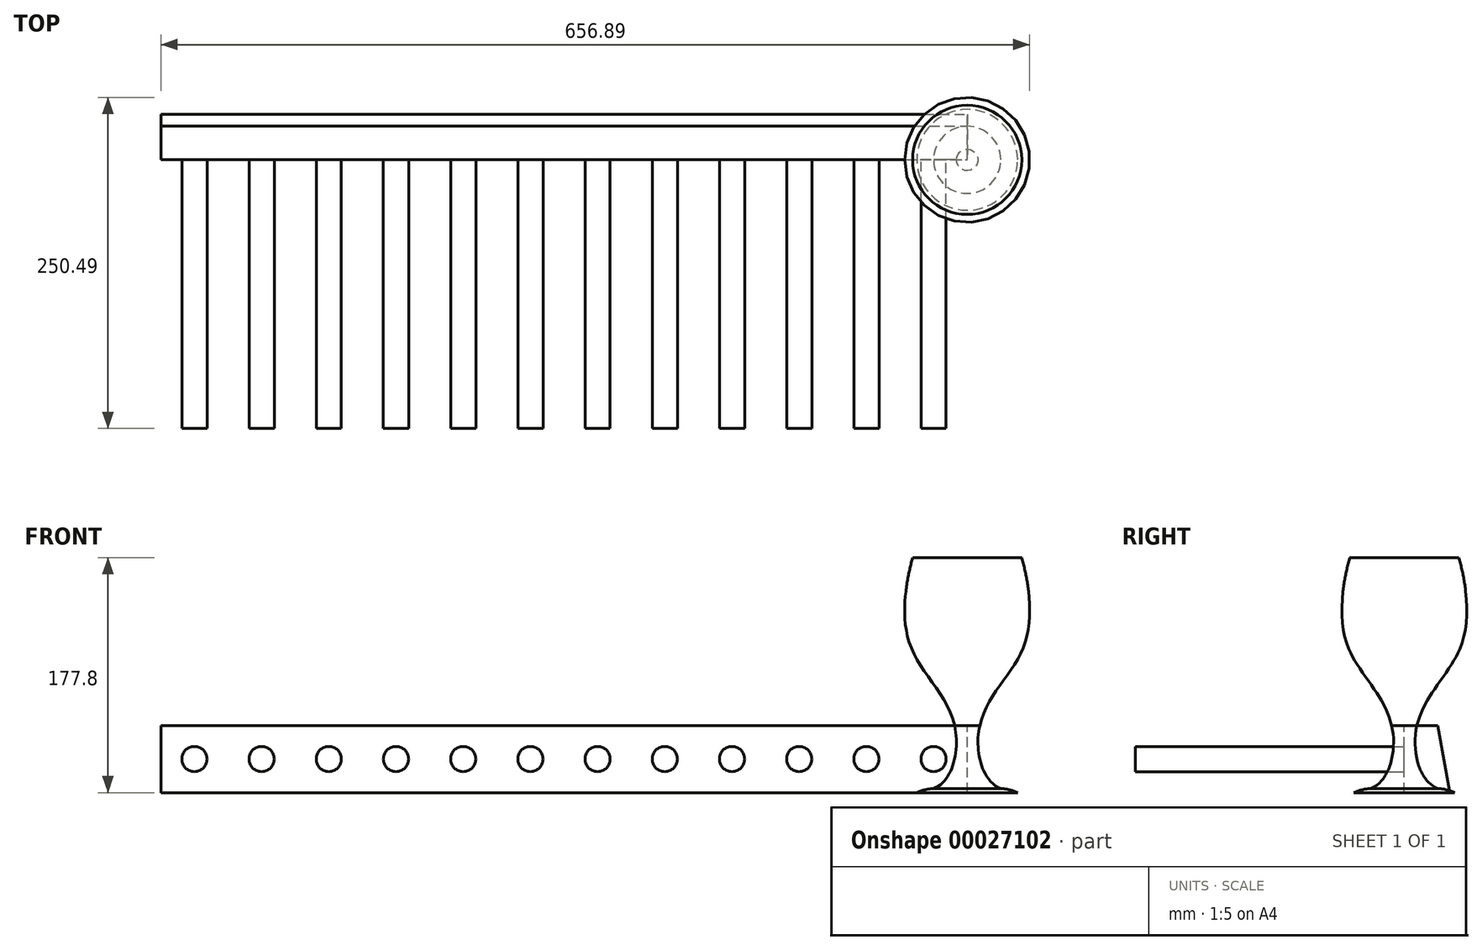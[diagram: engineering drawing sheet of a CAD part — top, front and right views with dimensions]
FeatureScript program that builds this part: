
annotation { "Feature Type Name" : "Feature", "Feature Type Description" : "" }
export const myFeature = defineFeature(function(context is Context, id is Id, definition is map)
    precondition{}
    {
        {
            var Q0;
            Q0=qCreatedBy(makeId("Front.planeOp"),FACE);
            var sketch = newSketch(context, id + "F0", { "sketchPlane" : qUnion([Q0])});
            skLineSegment(sketch, "E0", {"start": v(0, 0) * mm, "end": v(38.1, 0) * mm});
            skLineSegment(sketch, "E1", {"start": v(0, 0) * mm, "end": v(0, 177.8) * mm});
            skLineSegment(sketch, "E2", {"start": v(0, 177.8) * mm, "end": v(41.28, 177.8) * mm});
            skPoint(sketch, "E3", {"position": v(0, 152.4) * mm});
            skLineSegment(sketch, "E4", {"start": v(0, 152.4) * mm, "end": v(46.35, 152.4) * mm});
            skLineSegment(sketch, "E5", {"start": v(0, 50.8) * mm, "end": v(9.53, 50.8) * mm});
            skFitSpline(sketch, "E6", {"points": [v(41.28, 177.8) * mm, v(46.35, 152.4) * mm, v(41.28, 107.04) * mm, v(9.53, 50.8) * mm, v(25.4, 3.17) * mm], "startDerivative": vector(30.92, -120.33) * mm, "endDerivative": vector(160.95, -55.55) * mm});
            skArc(sketch, "E7", {"start": v(38.1, 0) * mm, "mid": v(31.89, 2.14) * mm, "end": v(25.4, 3.18) * mm});
            skPoint(sketch, "E8", {"position": v(9.53, 25.4) * mm});
            skSolve(sketch);
        }
        {
            var Q0;
            {var subQ2=sQuery(id+"F0.wireOp",EDGE,"E4");Q0=makeQuery(id+"F0.imprint","IMPRINT",FACE,{"disambiguationData":[TD([[makeQuery(id+"F0.imprint","IMPRINT",EDGE,{"derivedFrom":subQ2}),-1.0]])]});}
            var Q1;
            {var subQ2=sQuery(id+"F0.wireOp",EDGE,"E2");Q1=makeQuery(id+"F0.imprint","IMPRINT",FACE,{"disambiguationData":[TD([[makeQuery(id+"F0.imprint","IMPRINT",EDGE,{"derivedFrom":subQ2}),-1.0]])]});}
            var Q2;
            {var subQ4=sQuery(id+"F0.wireOp",EDGE,"E0");Q2=makeQuery(id+"F0.imprint","IMPRINT",FACE,{"disambiguationData":[TD([[makeQuery(id+"F0.imprint","IMPRINT",EDGE,{"derivedFrom":subQ4}),1.0]])]});}
            var Q3;
            Q3=sQuery(id+"F0.wireOp",EDGE,"E1");
            revolve(context, id + "F1", {"entities" : qUnion([Q0, Q1, Q2]), "axis" : qUnion([Q3]), "revolveType" : RevolveType.FULL});
        }
        {
            var Q0;
            Q0=qCreatedBy(makeId("Right.planeOp"),FACE);
            var sketch = newSketch(context, id + "F2", { "sketchPlane" : qUnion([Q0])});
            skLineSegment(sketch, "E9", {"start": v(0, 0) * mm, "end": v(0, 50.8) * mm});
            skLineSegment(sketch, "E10", {"start": v(0, 50.8) * mm, "end": v(25.4, 50.8) * mm});
            skLineSegment(sketch, "E11", {"start": v(25.4, 50.8) * mm, "end": v(34.36, 0) * mm});
            skLineSegment(sketch, "E12", {"start": v(34.36, 0) * mm, "end": v(0, 0) * mm});
            skSolve(sketch);
        }
        {
            var Q0;
            Q0=makeQuery(id+"F2.imprint","IMPRINT",FACE,{"disambiguationData":[TD([[makeQuery(id+"F2.imprint","IMPRINT",EDGE,{"derivedFrom":sQuery(id+"F2.wireOp",EDGE,"E9")}),-1.0]])]});
            extrude(context, id + "F3", {"entities" : qUnion([Q0]), "oppositeDirection" : true, "depth" : 609.6 * mm});
        }
        {
            var Q0;
            Q0=makeQuery(id+"F3.opExtrude","SWEPT_FACE",FACE,{"disambiguationData":[OSD([sQuery(id+"F2.wireOp",EDGE,"E9")])]});
            var sketch = newSketch(context, id + "F4", { "sketchPlane" : qUnion([Q0])});
            skCircle(sketch, "E13", {"center": v(-584.2, 25.4) * mm, "radius": 9.53 * mm});
            skCircle(sketch, "E14", {"center": v(-533.4, 25.4) * mm, "radius": 9.53 * mm});
            skCircle(sketch, "E15", {"center": v(-482.6, 25.4) * mm, "radius": 9.53 * mm});
            skCircle(sketch, "E16", {"center": v(-431.8, 25.4) * mm, "radius": 9.53 * mm});
            skCircle(sketch, "E17", {"center": v(-381, 25.4) * mm, "radius": 9.53 * mm});
            skCircle(sketch, "E18", {"center": v(-330.2, 25.4) * mm, "radius": 9.53 * mm});
            skCircle(sketch, "E19", {"center": v(-279.4, 25.4) * mm, "radius": 9.53 * mm});
            skCircle(sketch, "E20", {"center": v(-228.6, 25.4) * mm, "radius": 9.53 * mm});
            skCircle(sketch, "E21", {"center": v(-177.8, 25.4) * mm, "radius": 9.53 * mm});
            skCircle(sketch, "E22", {"center": v(-127, 25.4) * mm, "radius": 9.53 * mm});
            skCircle(sketch, "E23", {"center": v(-76.2, 25.4) * mm, "radius": 9.53 * mm});
            skCircle(sketch, "E24", {"center": v(-25.4, 25.4) * mm, "radius": 9.53 * mm});
            skSolve(sketch);
        }
        {
            var Q0;
            Q0 = qSketchRegion(id + "F4", true);
            extrude(context, id + "F5", {"entities" : qUnion([Q0]), "operationType" : NewBodyOperationType.REMOVE, "oppositeDirection" : true, "depth" : 25.4 * mm});
        }
        {
            var Q0;
            Q0=makeQuery(id+"F5.boolean.opBoolean","COPY",FACE,{"derivedFrom":makeQuery(id+"F5.opExtrude","CAP_FACE",FACE,{"disambiguationData":[OSD([sQuery(id+"F4.wireOp",EDGE,"E14")])],"isStart":false})});
            var Q1;
            Q1=makeQuery(id+"F5.boolean.opBoolean","COPY",FACE,{"derivedFrom":makeQuery(id+"F5.opExtrude","CAP_FACE",FACE,{"disambiguationData":[OSD([sQuery(id+"F4.wireOp",EDGE,"E15")])],"isStart":false})});
            var Q2;
            Q2=makeQuery(id+"F5.boolean.opBoolean","COPY",FACE,{"derivedFrom":makeQuery(id+"F5.opExtrude","CAP_FACE",FACE,{"disambiguationData":[OSD([sQuery(id+"F4.wireOp",EDGE,"E16")])],"isStart":false})});
            var Q3;
            Q3=makeQuery(id+"F5.boolean.opBoolean","COPY",FACE,{"derivedFrom":makeQuery(id+"F5.opExtrude","CAP_FACE",FACE,{"disambiguationData":[OSD([sQuery(id+"F4.wireOp",EDGE,"E17")])],"isStart":false})});
            var Q4;
            Q4=makeQuery(id+"F5.boolean.opBoolean","COPY",FACE,{"derivedFrom":makeQuery(id+"F5.opExtrude","CAP_FACE",FACE,{"disambiguationData":[OSD([sQuery(id+"F4.wireOp",EDGE,"E18")])],"isStart":false})});
            var Q5;
            Q5=makeQuery(id+"F5.boolean.opBoolean","COPY",FACE,{"derivedFrom":makeQuery(id+"F5.opExtrude","CAP_FACE",FACE,{"disambiguationData":[OSD([sQuery(id+"F4.wireOp",EDGE,"E13")])],"isStart":false})});
            var Q6;
            Q6=makeQuery(id+"F5.boolean.opBoolean","COPY",FACE,{"derivedFrom":makeQuery(id+"F5.opExtrude","CAP_FACE",FACE,{"disambiguationData":[OSD([sQuery(id+"F4.wireOp",EDGE,"E19")])],"isStart":false})});
            var Q7;
            Q7=makeQuery(id+"F5.boolean.opBoolean","COPY",FACE,{"derivedFrom":makeQuery(id+"F5.opExtrude","CAP_FACE",FACE,{"disambiguationData":[OSD([sQuery(id+"F4.wireOp",EDGE,"E20")])],"isStart":false})});
            var Q8;
            Q8=makeQuery(id+"F5.boolean.opBoolean","COPY",FACE,{"derivedFrom":makeQuery(id+"F5.opExtrude","CAP_FACE",FACE,{"disambiguationData":[OSD([sQuery(id+"F4.wireOp",EDGE,"E21")])],"isStart":false})});
            var Q9;
            Q9=makeQuery(id+"F5.boolean.opBoolean","COPY",FACE,{"derivedFrom":makeQuery(id+"F5.opExtrude","CAP_FACE",FACE,{"disambiguationData":[OSD([sQuery(id+"F4.wireOp",EDGE,"E22")])],"isStart":false})});
            var Q10;
            Q10=makeQuery(id+"F5.boolean.opBoolean","COPY",FACE,{"derivedFrom":makeQuery(id+"F5.opExtrude","CAP_FACE",FACE,{"disambiguationData":[OSD([sQuery(id+"F4.wireOp",EDGE,"E23")])],"isStart":false})});
            var Q11;
            Q11=makeQuery(id+"F5.boolean.opBoolean","COPY",FACE,{"derivedFrom":makeQuery(id+"F5.opExtrude","CAP_FACE",FACE,{"disambiguationData":[OSD([sQuery(id+"F4.wireOp",EDGE,"E24")])],"isStart":false})});
            extrude(context, id + "F6", {"entities" : qUnion([Q0, Q1, Q2, Q3, Q4, Q5, Q6, Q7, Q8, Q9, Q10, Q11]), "operationType" : NewBodyOperationType.ADD, "depth" : 228.6 * mm});
        }
    });
